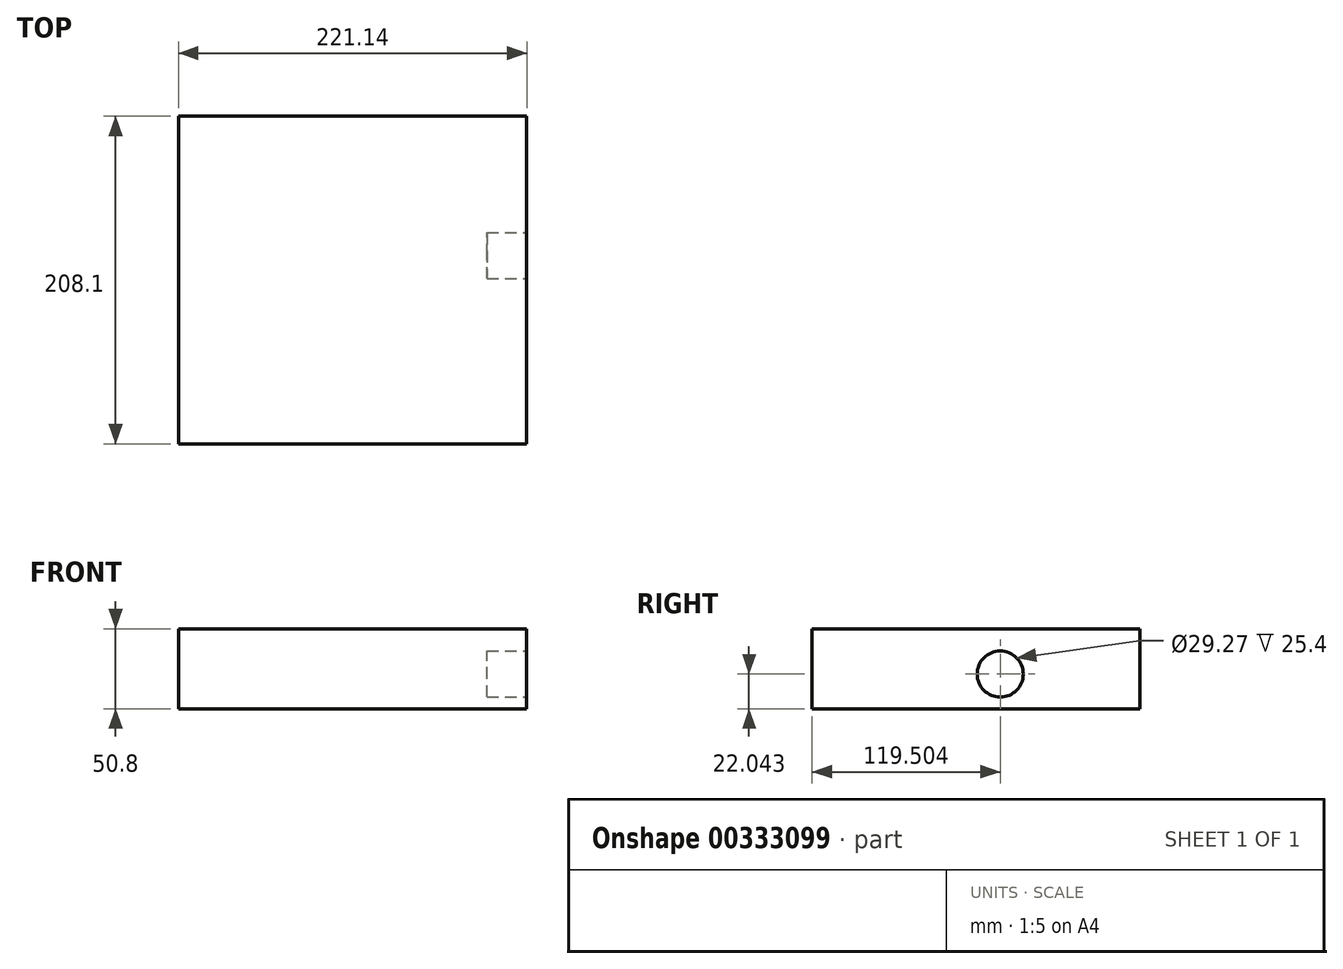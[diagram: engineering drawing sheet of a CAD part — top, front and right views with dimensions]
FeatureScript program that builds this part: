
annotation { "Feature Type Name" : "Feature", "Feature Type Description" : "" }
export const myFeature = defineFeature(function(context is Context, id is Id, definition is map)
    precondition{}
    {
        {
            var Q0;
            Q0=qCreatedBy(makeId("Top.planeOp"),FACE);
            var sketch = newSketch(context, id + "F0", { "sketchPlane" : qUnion([Q0])});
            skLineSegment(sketch, "E0.bottom", {"start": v(110.57, 104.05) * mm, "end": v(-110.57, 104.05) * mm});
            skLineSegment(sketch, "E0.top", {"start": v(110.57, -104.05) * mm, "end": v(-110.57, -104.05) * mm});
            skLineSegment(sketch, "E0.left", {"start": v(110.57, 104.05) * mm, "end": v(110.57, -104.05) * mm});
            skLineSegment(sketch, "E0.right", {"start": v(-110.57, 104.05) * mm, "end": v(-110.57, -104.05) * mm});
            skPoint(sketch, "E0.middle", {"position": v(0, 0) * mm});
            skSolve(sketch);
        }
        {
            var Q0;
            Q0=qSketchRegion(id+"F0",true);
            extrude(context, id + "F1", {"entities" : qUnion([Q0]), "depth" : 50.8 * mm});
        }
        {
            var Q0;
            Q0=makeQuery(id+"F1.opExtrude","SWEPT_FACE",FACE,{"disambiguationData":[OSD([sQuery(id+"F0.wireOp",EDGE,"E0.left")])]});
            var sketch = newSketch(context, id + "F2", { "sketchPlane" : qUnion([Q0])});
            skCircle(sketch, "E1", {"center": v(15.45, 22.04) * mm, "radius": 14.64 * mm});
            skSolve(sketch);
        }
        {
            var Q0;
            Q0=qSketchRegion(id+"F2",true);
            extrude(context, id + "F3", {"entities" : qUnion([Q0]), "operationType" : NewBodyOperationType.REMOVE, "oppositeDirection" : true, "depth" : 25.4 * mm});
        }
    });
